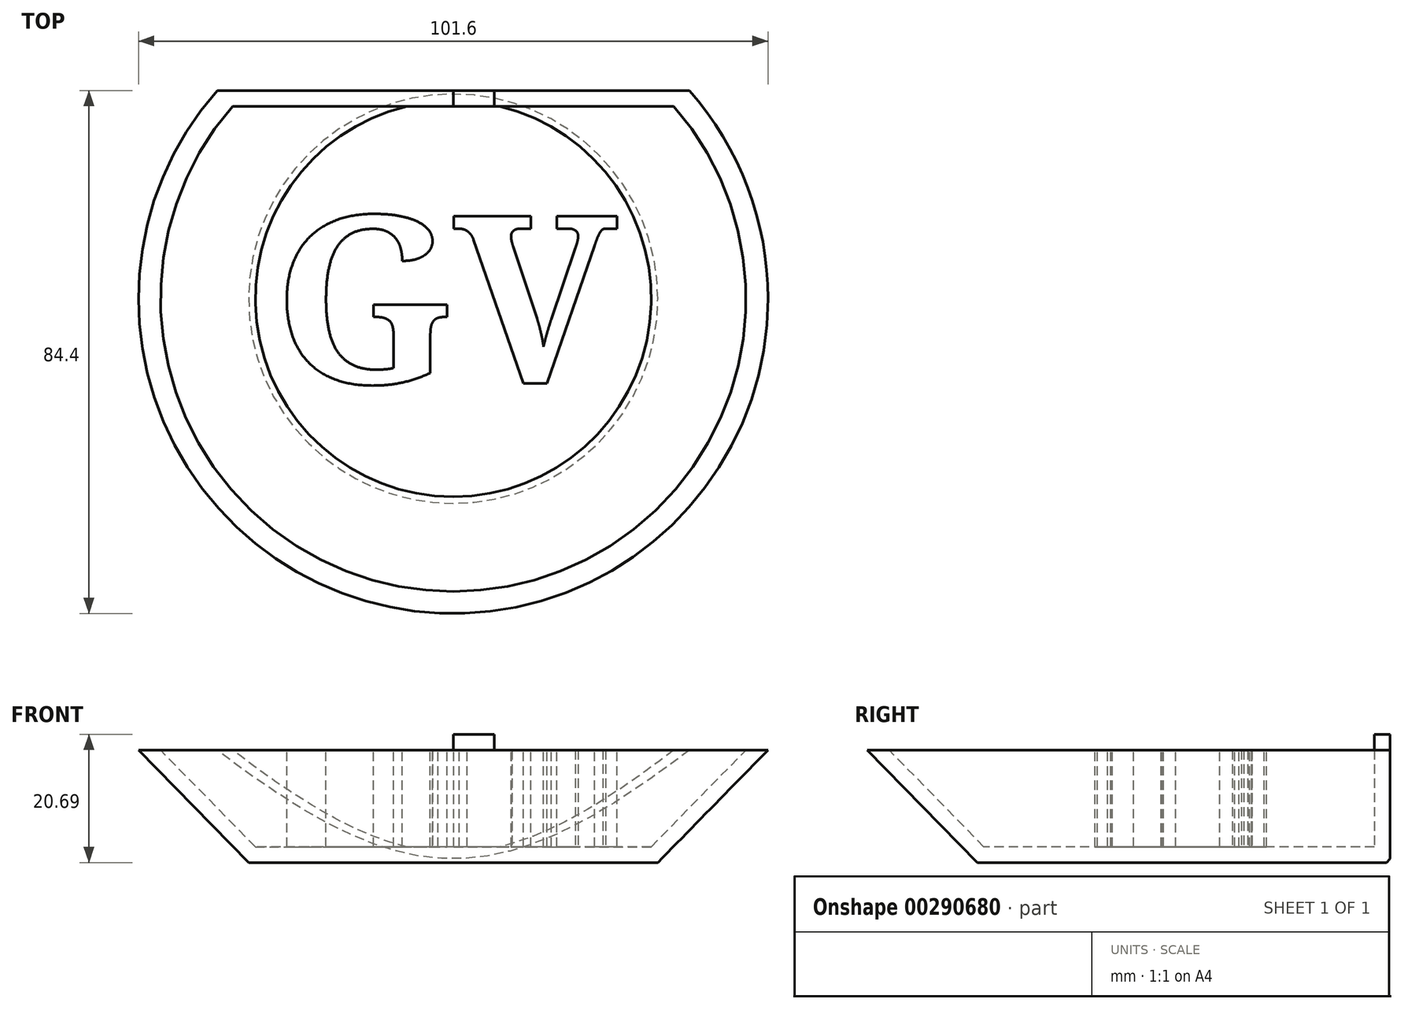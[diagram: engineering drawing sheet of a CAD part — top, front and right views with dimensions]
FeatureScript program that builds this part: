
annotation { "Feature Type Name" : "Feature", "Feature Type Description" : "" }
export const myFeature = defineFeature(function(context is Context, id is Id, definition is map)
    precondition{}
    {
        {
            var Q0;
            Q0=qCreatedBy(makeId("Front.planeOp"),FACE);
            var sketch = newSketch(context, id + "F0", { "sketchPlane" : qUnion([Q0])});
            skLineSegment(sketch, "E0", {"start": v(0, 0) * mm, "end": v(-50.8, 0) * mm});
            skLineSegment(sketch, "E1", {"start": v(-50.8, 0) * mm, "end": v(-33.02, -18.14) * mm});
            skLineSegment(sketch, "E2", {"start": v(-33.02, -18.14) * mm, "end": v(0, -18.14) * mm});
            skLineSegment(sketch, "E3", {"start": v(0, 0) * mm, "end": v(0, -18.14) * mm});
            skSolve(sketch);
        }
        {
            var Q0;
            Q0=makeQuery(id+"F0.imprint","IMPRINT",FACE,{"disambiguationData":[TD([[makeQuery(id+"F0.imprint","IMPRINT",EDGE,{"derivedFrom":sQuery(id+"F0.wireOp",EDGE,"E0")}),1.0]])]});
            var Q1;
            Q1=sQuery(id+"F0.wireOp",EDGE,"E3");
            revolve(context, id + "F1", {"entities" : qUnion([Q0]), "axis" : qUnion([Q1]), "revolveType" : RevolveType.FULL});
        }
        {
            var Q0;
            Q0=qCreatedBy(makeId("Top.planeOp"),FACE);
            var sketch = newSketch(context, id + "F2", { "sketchPlane" : qUnion([Q0])});
            skCircle(sketch, "E4.0", {"center": v(0, 0) * mm, "radius": 50.8 * mm});
            skLineSegment(sketch, "E5", {"start": v(-38.1, 33.6) * mm, "end": v(38.1, 33.6) * mm});
            skSolve(sketch);
        }
        {
            var Q0;
            {var subQ0=sQuery(id+"F2.wireOp",EDGE,"E5");Q0=makeQuery(id+"F2.imprint","IMPRINT",FACE,{"disambiguationData":[TD([[makeQuery(id+"F2.imprint","IMPRINT",EDGE,{"derivedFrom":subQ0}),1.0]])]});}
            extrude(context, id + "F3", {"entities" : qUnion([Q0]), "operationType" : NewBodyOperationType.REMOVE, "oppositeDirection" : true, "depth" : 25.4 * mm});
        }
        {
            var Q0;
            Q0=makeQuery(id+"F1.opRevolve","SWEPT_FACE",FACE,{"disambiguationData":[OSD([sQuery(id+"F0.wireOp",EDGE,"E0")])]});
            shell(context, id + "F4", {"entities" : qUnion([Q0]), "thickness" : 2.54 * mm});
        }
        {
            var Q0;
            Q0=makeQuery(id+"F1.opRevolve","SWEPT_FACE",FACE,{"disambiguationData":[OSD([sQuery(id+"F0.wireOp",EDGE,"E0")])]});
            var sketch = newSketch(context, id + "F5", { "sketchPlane" : qUnion([Q0])});
            skArc(sketch, "E6.0", {"start": v(-7.5, 31.06) * mm, "mid": v(0, -31.95) * mm, "end": v(7.5, 31.06) * mm});
            skText(sketch, "E7", { "text": "GV\n", "fontName": "NotoSerif-Bold.ttf"});
            const initialGuessF5  = {"E7": [-0.02895, -0.01365, 1, 0, 0.02718]};
            skSetInitialGuess(sketch, initialGuessF5);
            skSolve(sketch);
        }
        {
            var Q0;
            Q0=makeQuery(id+"F5.imprint","IMPRINT",FACE,{"disambiguationData":[TD([[makeQuery(id+"F5.imprint","IMPRINT",EDGE,{"derivedFrom":sQuery(id+"F5.wireOp",EDGE,"E7.sketch_text.stroke-45")}),-1.0]])]});
            var Q1;
            Q1=makeQuery(id+"F5.imprint","IMPRINT",FACE,{"disambiguationData":[TD([[makeQuery(id+"F5.imprint","IMPRINT",EDGE,{"derivedFrom":sQuery(id+"F5.wireOp",EDGE,"E7.sketch_text.stroke-0")}),-1.0]])]});
            extrude(context, id + "F6", {"entities" : qUnion([Q0, Q1]), "endBound" : BoundingType.UP_TO_NEXT, "oppositeDirection" : true, "depth" : 13.97 * mm});
        }
        {
            var Q0;
            Q0=makeQuery(id+"F3.boolean.opBoolean","COPY",FACE,{"derivedFrom":makeQuery(id+"F3.opExtrude","SWEPT_FACE",FACE,{"disambiguationData":[OSD([sQuery(id+"F2.wireOp",EDGE,"E5")])]})});
            var sketch = newSketch(context, id + "F7", { "sketchPlane" : qUnion([Q0])});
            skLineSegment(sketch, "E8.0", {"start": v(38.1, 0) * mm, "end": v(-38.1, 0) * mm});
            skLineSegment(sketch, "E9", {"start": v(-6.61, 0) * mm, "end": v(-6.61, 2.55) * mm});
            skLineSegment(sketch, "E10", {"start": v(-6.61, 2.55) * mm, "end": v(0, 2.55) * mm});
            skLineSegment(sketch, "E11", {"start": v(0, 2.55) * mm, "end": v(0, 0) * mm});
            skSolve(sketch);
        }
        {
            var Q0;
            {var subQ0=sQuery(id+"F7.wireOp",EDGE,"E9");Q0=makeQuery(id+"F7.imprint","IMPRINT",FACE,{"disambiguationData":[TD([[makeQuery(id+"F7.imprint","IMPRINT",EDGE,{"derivedFrom":subQ0}),-1.0]])]});}
            extrude(context, id + "F8", {"entities" : qUnion([Q0]), "operationType" : NewBodyOperationType.ADD, "oppositeDirection" : true, "depth" : 2.54 * mm});
        }
    });
